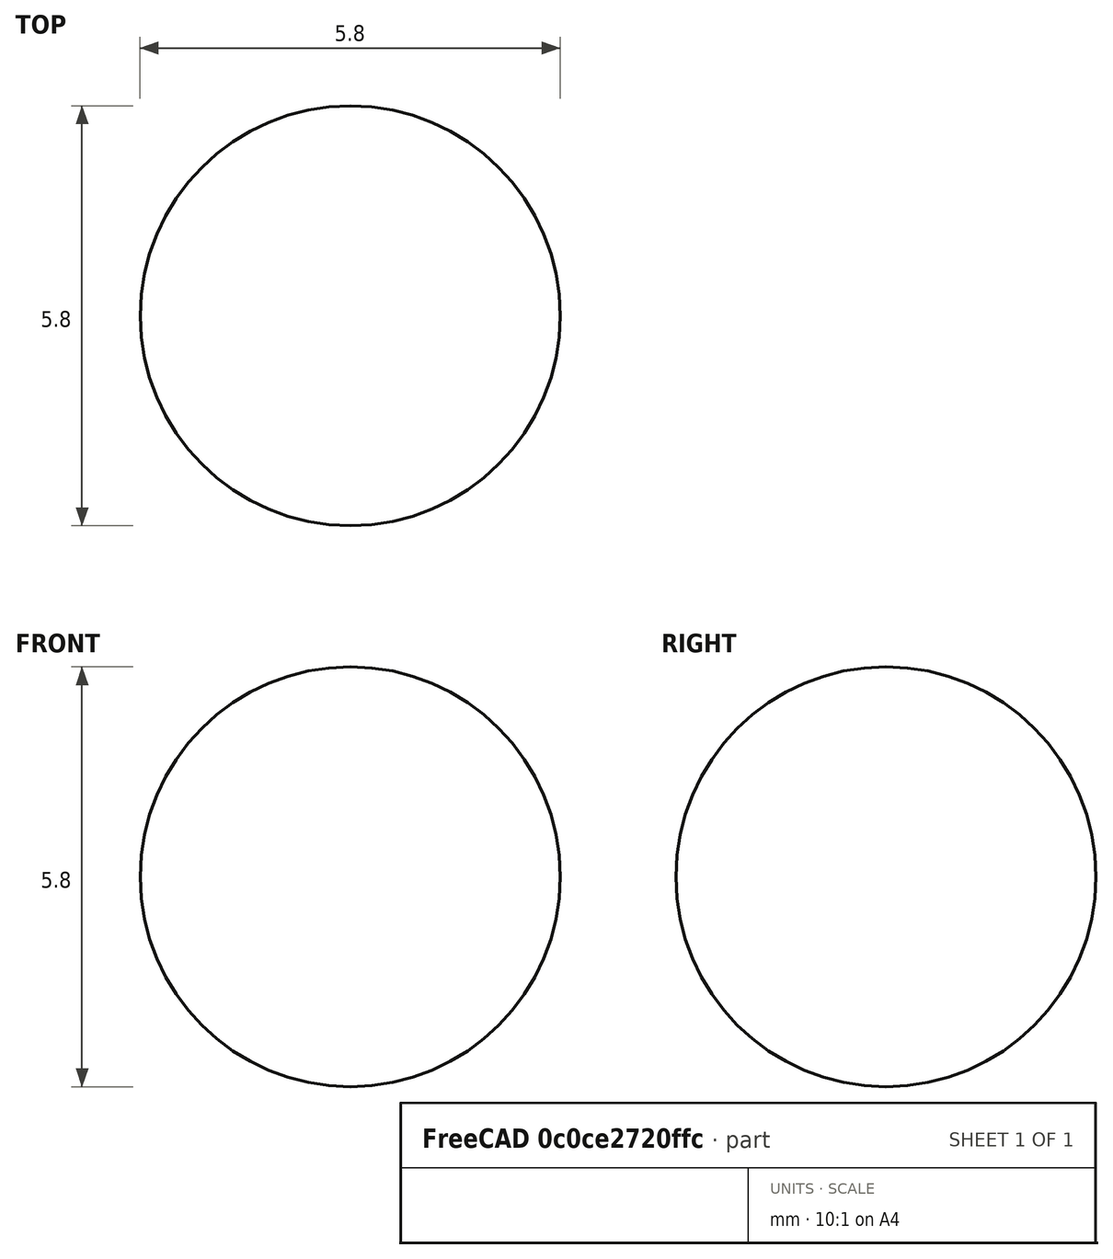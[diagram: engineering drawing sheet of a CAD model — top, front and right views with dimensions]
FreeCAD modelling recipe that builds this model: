
FCSTD DOCUMENT  (FreeCAD 0.18R16131 (Git))
Label: CORAÇÃO_CURVA PARAMETRICA
License: All rights reserved
LicenseURL: http://en.wikipedia.org/wiki/All_rights_reserved
objects: Part::Part2DObjectPython×2, App::DocumentObjectGroupPython×2, Part::Vertex×1, Part::Circle×1, Part::Compound×1, Part::Sweep×1, Part::Feature×1, Part::FeaturePython×1, Part::Sphere×1
note: 9 computed .brp shape members not serialized (recipe doc carries the construction recipe); baked Part::Feature solids carry a one-line shape summary decoded from their .brp

FEATURE [Part::Vertex] Vertex
  AttacherType = Attacher::AttachEngine3D
  X = 0
  Y = 0
  Z = 0
FEATURE [Part::Circle] Circle
  Angle0 = 0
  Angle1 = 360
  AttacherType = Attacher::AttachEngine3D
  Radius = 3
FEATURE [Part::Compound] Compound
  Links = -> [Vertex,Circle]
  Placement = pos=(0,8,0) rot=(0,0,1;4.71239rad)
FEATURE [Part::Part2DObjectPython] BSpline  # Draft 2D object (typed FeaturePython)
  Closed = false
  MakeFace = false
  Parameterization = 1
  Points = (18) [(0,8,0),(0.49218,10.68,0),(2.99427,16.105,0),(8.28772,21.5713,0),(13.506,23.9436,0),(19.2612,24.2842,0),(22.6356,23.426,0),(27.5276,20.3607,0),+10 more]
FEATURE [Part::Part2DObjectPython] Circle001  # Draft 2D object (typed FeaturePython)
  FirstAngle = 0
  LastAngle = 0
  MakeFace = false
  Placement = pos=(0,8,0) rot=(1,0,0;1.5708rad)
  Radius = 2.99878
FEATURE [Part::Sweep] Sweep
  Frenet = false
  Sections = -> [Circle001]
  Solid = false
  Spine = -> BSpline [Edge1]
  Transition = 1
FEATURE [Part::Feature] Sweep001
  Placement = pos=(0,0,0) rot=(0,1,0;3.14159rad)
  shape: bbox 48.53 x 69.29 x 11.4 mm, 1 faces, 0 solids (baked)
FEATURE [Part::FeaturePython] BooleanFragments  # WARN: FeaturePython — macro-defined, semantics opaque (R4)
  Mode = 0
  Objects = -> [Sweep001,Sweep]
  Tolerance = 0
FEATURE [Part::Sphere] Sphere
  Angle1 = -90
  Angle2 = 90
  Angle3 = 360
  AttacherType = Attacher::AttachEngine3D
  Placement = pos=(4.92293,18.6194,0) rot=(0,0,1;4.1469rad)
  Radius = 2.9
FEATURE [App::DocumentObjectGroupPython] My_Placer  # scripted group (container) (typed FeaturePython)
  Placement = pos=(4.92293,18.6194,0) rot=(0,0,1;10.4301rad)
  RotAxis = (0,0,1)
  RotCenter = (0,0,0)
  arc = 270+time*180
  arc0 = 0
  arc1 = 90
  target = -> Sphere
  time = 1.82
  x = -32*x0**3
  x0 = -0.535827
  x1 = 0.844328
  y = 26*x1-12*y0-4*y1-2*z0
  y0 = 0.425779
  y1 = -0.125333
  z = 0
  z0 = -0.637424
  z1 = 0
  expr: y1 = cos(time * 180 * 3)
  expr: z0 = cos(time * 180 * 4)
  expr: x1 = cos(time * 180 * 1)
  expr: y0 = cos(time * 180 * 2)
  expr: x0 = sin(time * 180)
FEATURE [App::DocumentObjectGroupPython] My_Manager  # scripted group (container) (typed FeaturePython)
  Group = -> [My_Placer]
  intervall = 400
  sleeptime = 0.02
  start = 0
  step = 183
  text = NO
